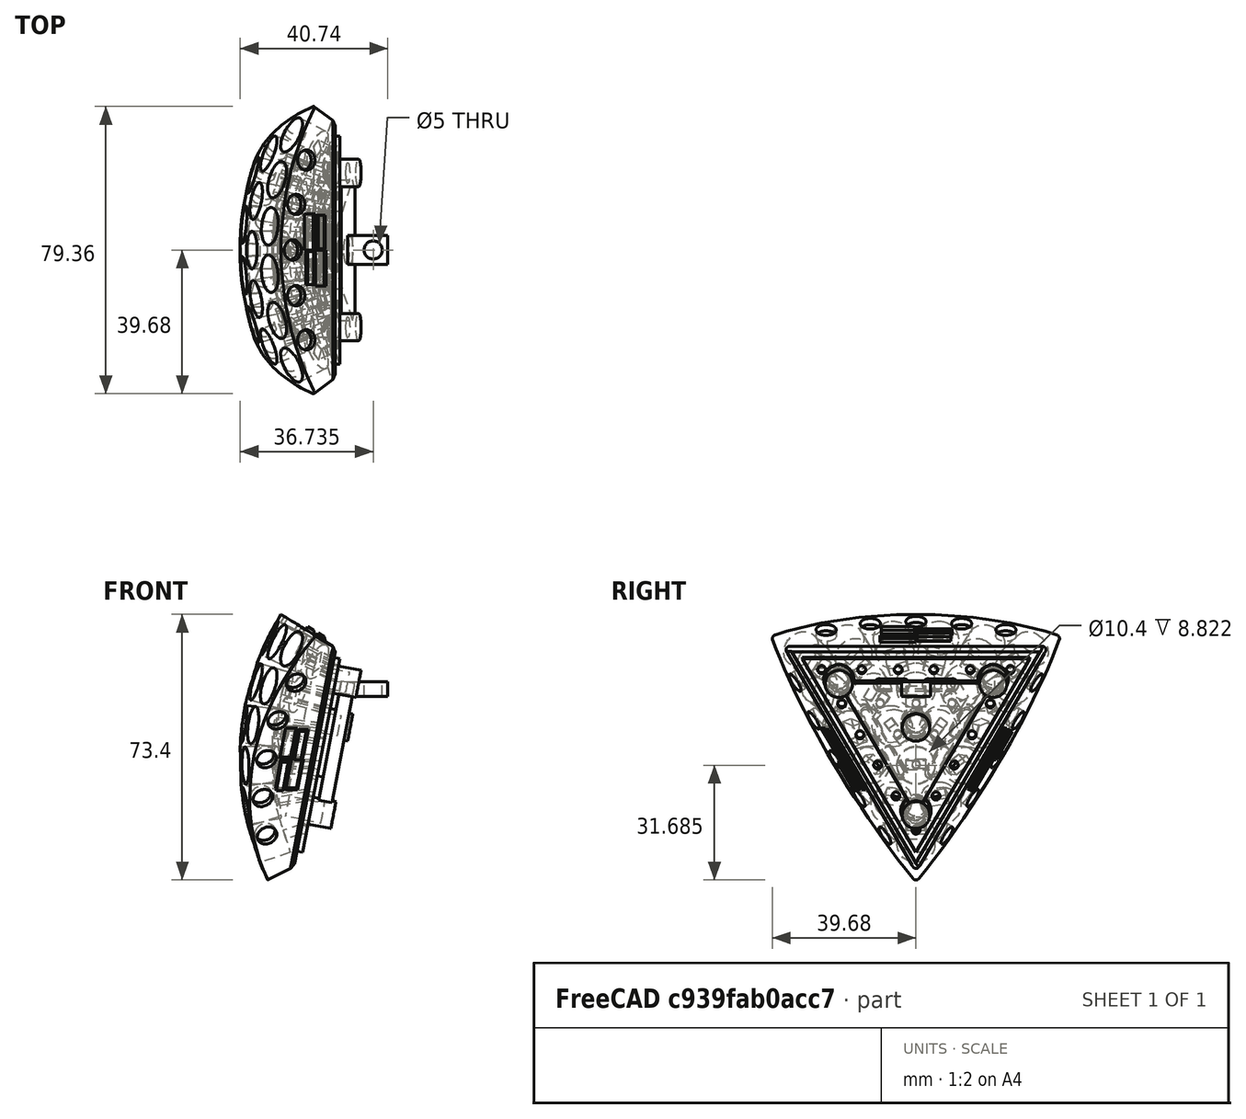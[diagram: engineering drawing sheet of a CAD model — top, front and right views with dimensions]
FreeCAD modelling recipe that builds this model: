
FCSTD DOCUMENT  (FreeCAD 0.19R24267 +99 (Git))
Label: Shell_rev1
License: All rights reserved
LicenseURL: http://en.wikipedia.org/wiki/All_rights_reserved
objects: Part::Feature×3, Part::Chamfer×3, Part::Part2DObjectPython×1, Part::Fillet×1
note: 8 computed .brp shape members not serialized (recipe doc carries the construction recipe); baked Part::Feature solids carry a one-line shape summary decoded from their .brp

FEATURE [Part::Part2DObjectPython] Line  # Draft 2D object (typed FeaturePython)
  Area = 0
  ChamferSize = 0
  Closed = false
  End = (-60.4609,0,-2.48e-14)
  FilletRadius = 0
  Length = 60.4609
  MakeFace = true
  Points = (2) [(0,0,0),(-60.4609,0,-2.4803e-14)]
  Start = (0,0,0)
  Subdivisions = 0
FEATURE [Part::Feature] Shape
  Placement = pos=(0,0,0) rot=(0,1,0;0.188711rad)
  shape: bbox 26.49 x 83.96 x 75.99 mm, 229 faces (baked)
FEATURE [Part::Feature] Shape001
  Placement = pos=(0,0,0) rot=(0,1,0;0.188711rad)
  shape: bbox 11.8 x 62.95 x 53.85 mm, 54 faces (baked)
FEATURE [Part::Feature] Shape002
  shape: bbox 23.55 x 50.22 x 45.22 mm, 59 faces (baked)
FEATURE [Part::Fillet] Fillet
  Base = -> Shape
  Edges = 3 edges r=1: [Edge25,Edge27,Edge50]
FEATURE [Part::Chamfer] Chamfer
  Base = -> Fillet
  Edges = 1 edges r=1: [Edge79]
FEATURE [Part::Chamfer] Chamfer001
  Base = -> Chamfer
  Edges = 4 edges r=0.4: [Edge150,Edge171,Edge184,Edge225]
FEATURE [Part::Chamfer] Chamfer002
  Base = -> Chamfer001
  Edges = 6 edges r=0.8: [Edge443,Edge453,Edge487,Edge499,Edge530,Edge542]
